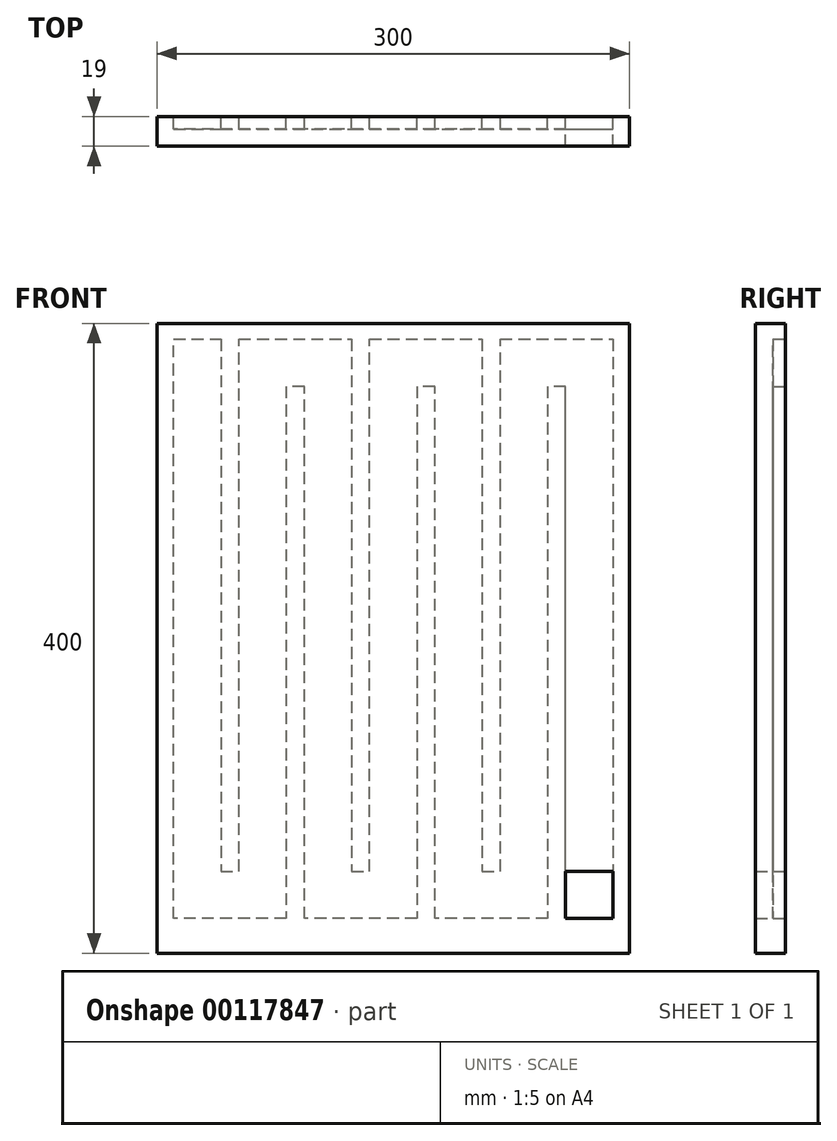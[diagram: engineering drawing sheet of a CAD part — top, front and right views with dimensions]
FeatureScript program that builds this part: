
annotation { "Feature Type Name" : "Feature", "Feature Type Description" : "" }
export const myFeature = defineFeature(function(context is Context, id is Id, definition is map)
    precondition{}
    {
        {
            var Q0;
            Q0=qCreatedBy(makeId("Front.planeOp"),FACE);
            var sketch = newSketch(context, id + "F0", { "sketchPlane" : qUnion([Q0])});
            skLineSegment(sketch, "E0.bottom", {"start": v(-152.58, 165.2) * mm, "end": v(147.42, 165.2) * mm});
            skLineSegment(sketch, "E0.top", {"start": v(-152.58, -234.8) * mm, "end": v(147.42, -234.8) * mm});
            skLineSegment(sketch, "E0.left", {"start": v(-152.58, 165.2) * mm, "end": v(-152.58, -234.8) * mm});
            skLineSegment(sketch, "E0.right", {"start": v(147.42, 165.2) * mm, "end": v(147.42, -234.8) * mm});
            skSolve(sketch);
        }
        {
            var Q0;
            Q0 = qSketchRegion(id + "F0", true);
            extrude(context, id + "F1", {"entities" : qUnion([Q0]), "depth" : 19 * mm});
        }
        {
            var Q0;
            Q0=makeQuery(id+"F1.opExtrude","CAP_FACE",FACE,{"disambiguationData":[OSD([sQuery(id+"F0.wireOp",EDGE,"E0.bottom"),sQuery(id+"F0.wireOp",EDGE,"E0.top"),sQuery(id+"F0.wireOp",EDGE,"E0.left"),sQuery(id+"F0.wireOp",EDGE,"E0.right")])],"isStart":true});
            var sketch = newSketch(context, id + "F2", { "sketchPlane" : qUnion([Q0])});
            skLineSegment(sketch, "E1", {"start": v(-136.92, -212.8) * mm, "end": v(-106.92, -212.8) * mm});
            skLineSegment(sketch, "E2", {"start": v(-106.92, -212.8) * mm, "end": v(-106.92, 125.2) * mm});
            skLineSegment(sketch, "E3", {"start": v(-106.92, 125.2) * mm, "end": v(-95.42, 125.2) * mm});
            skLineSegment(sketch, "E4", {"start": v(-95.42, 125.2) * mm, "end": v(-95.42, -212.8) * mm});
            skLineSegment(sketch, "E5", {"start": v(-95.42, -212.8) * mm, "end": v(-23.92, -212.8) * mm});
            skLineSegment(sketch, "E6", {"start": v(-23.92, -212.8) * mm, "end": v(-23.92, 125.2) * mm});
            skLineSegment(sketch, "E7", {"start": v(-23.92, 125.2) * mm, "end": v(-12.42, 125.2) * mm});
            skLineSegment(sketch, "E8", {"start": v(-12.42, 125.2) * mm, "end": v(-12.42, -212.8) * mm});
            skLineSegment(sketch, "E9", {"start": v(-12.42, -212.8) * mm, "end": v(59.08, -212.8) * mm});
            skLineSegment(sketch, "E10", {"start": v(59.08, -212.8) * mm, "end": v(59.08, 125.2) * mm});
            skLineSegment(sketch, "E11", {"start": v(59.08, 125.2) * mm, "end": v(70.58, 125.2) * mm});
            skLineSegment(sketch, "E12", {"start": v(70.58, 125.2) * mm, "end": v(70.58, -212.8) * mm});
            skLineSegment(sketch, "E13", {"start": v(70.58, -212.8) * mm, "end": v(142.08, -212.8) * mm});
            skLineSegment(sketch, "E14", {"start": v(142.08, -212.8) * mm, "end": v(142.08, 155.2) * mm});
            skLineSegment(sketch, "E15", {"start": v(142.08, 155.2) * mm, "end": v(112.08, 155.2) * mm});
            skLineSegment(sketch, "E16", {"start": v(112.08, 155.2) * mm, "end": v(112.08, -182.8) * mm});
            skLineSegment(sketch, "E17", {"start": v(112.08, -182.8) * mm, "end": v(100.58, -182.8) * mm});
            skLineSegment(sketch, "E18", {"start": v(100.58, -182.8) * mm, "end": v(100.58, 155.2) * mm});
            skLineSegment(sketch, "E19", {"start": v(100.58, 155.2) * mm, "end": v(29.08, 155.2) * mm});
            skLineSegment(sketch, "E20", {"start": v(29.08, 155.2) * mm, "end": v(29.08, -182.8) * mm});
            skLineSegment(sketch, "E21", {"start": v(29.08, -182.8) * mm, "end": v(17.58, -182.8) * mm});
            skLineSegment(sketch, "E22", {"start": v(17.58, -182.8) * mm, "end": v(17.58, 155.2) * mm});
            skLineSegment(sketch, "E23", {"start": v(17.58, 155.2) * mm, "end": v(-53.92, 155.2) * mm});
            skLineSegment(sketch, "E24", {"start": v(-53.92, 155.2) * mm, "end": v(-53.92, -182.8) * mm});
            skLineSegment(sketch, "E25", {"start": v(-53.92, -182.8) * mm, "end": v(-65.42, -182.8) * mm});
            skLineSegment(sketch, "E26", {"start": v(-65.42, -182.8) * mm, "end": v(-65.42, 155.2) * mm});
            skLineSegment(sketch, "E27", {"start": v(-65.42, 155.2) * mm, "end": v(-136.92, 155.2) * mm});
            skLineSegment(sketch, "E28", {"start": v(-136.92, 155.2) * mm, "end": v(-136.92, -212.8) * mm});
            skSolve(sketch);
        }
        {
            var Q0;
            Q0 = qSketchRegion(id + "F2", true);
            extrude(context, id + "F3", {"entities" : qUnion([Q0]), "operationType" : NewBodyOperationType.REMOVE, "oppositeDirection" : true, "depth" : 8 * mm});
        }
        {
            var Q0;
            Q0=makeQuery(id+"F3.boolean.opBoolean","COPY",FACE,{"derivedFrom":makeQuery(id+"F3.opExtrude","CAP_FACE",FACE,{"disambiguationData":[OSD([sQuery(id+"F2.wireOp",EDGE,"E1"),sQuery(id+"F2.wireOp",EDGE,"E2"),sQuery(id+"F2.wireOp",EDGE,"E3"),sQuery(id+"F2.wireOp",EDGE,"E4"),sQuery(id+"F2.wireOp",EDGE,"E5"),sQuery(id+"F2.wireOp",EDGE,"E6"),sQuery(id+"F2.wireOp",EDGE,"E7"),sQuery(id+"F2.wireOp",EDGE,"E8"),sQuery(id+"F2.wireOp",EDGE,"E9"),sQuery(id+"F2.wireOp",EDGE,"E10"),sQuery(id+"F2.wireOp",EDGE,"E11"),sQuery(id+"F2.wireOp",EDGE,"E12"),sQuery(id+"F2.wireOp",EDGE,"E13"),sQuery(id+"F2.wireOp",EDGE,"E14"),sQuery(id+"F2.wireOp",EDGE,"E15"),sQuery(id+"F2.wireOp",EDGE,"E16"),sQuery(id+"F2.wireOp",EDGE,"E17"),sQuery(id+"F2.wireOp",EDGE,"E18"),sQuery(id+"F2.wireOp",EDGE,"E19"),sQuery(id+"F2.wireOp",EDGE,"E20"),sQuery(id+"F2.wireOp",EDGE,"E21"),sQuery(id+"F2.wireOp",EDGE,"E22"),sQuery(id+"F2.wireOp",EDGE,"E23"),sQuery(id+"F2.wireOp",EDGE,"E24"),sQuery(id+"F2.wireOp",EDGE,"E25"),sQuery(id+"F2.wireOp",EDGE,"E26"),sQuery(id+"F2.wireOp",EDGE,"E27"),sQuery(id+"F2.wireOp",EDGE,"E28")])],"isStart":false})});
            var sketch = newSketch(context, id + "F4", { "sketchPlane" : qUnion([Q0])});
            skLineSegment(sketch, "E29.bottom", {"start": v(-106.92, -212.8) * mm, "end": v(-136.92, -212.8) * mm});
            skLineSegment(sketch, "E29.top", {"start": v(-106.92, -182.8) * mm, "end": v(-136.92, -182.8) * mm});
            skLineSegment(sketch, "E29.left", {"start": v(-106.92, -212.8) * mm, "end": v(-106.92, -182.8) * mm});
            skLineSegment(sketch, "E29.right", {"start": v(-136.92, -212.8) * mm, "end": v(-136.92, -182.8) * mm});
            skSolve(sketch);
        }
        {
            var Q0;
            Q0 = qSketchRegion(id + "F4", true);
            extrude(context, id + "F5", {"entities" : qUnion([Q0]), "operationType" : NewBodyOperationType.ADD, "oppositeDirection" : true, "depth" : 11 * mm});
        }
        {
            var Q0;
            Q0 = qSketchRegion(id + "F4", true);
            extrude(context, id + "F6", {"entities" : qUnion([Q0]), "operationType" : NewBodyOperationType.REMOVE, "oppositeDirection" : true, "depth" : 11 * mm});
        }
    });
